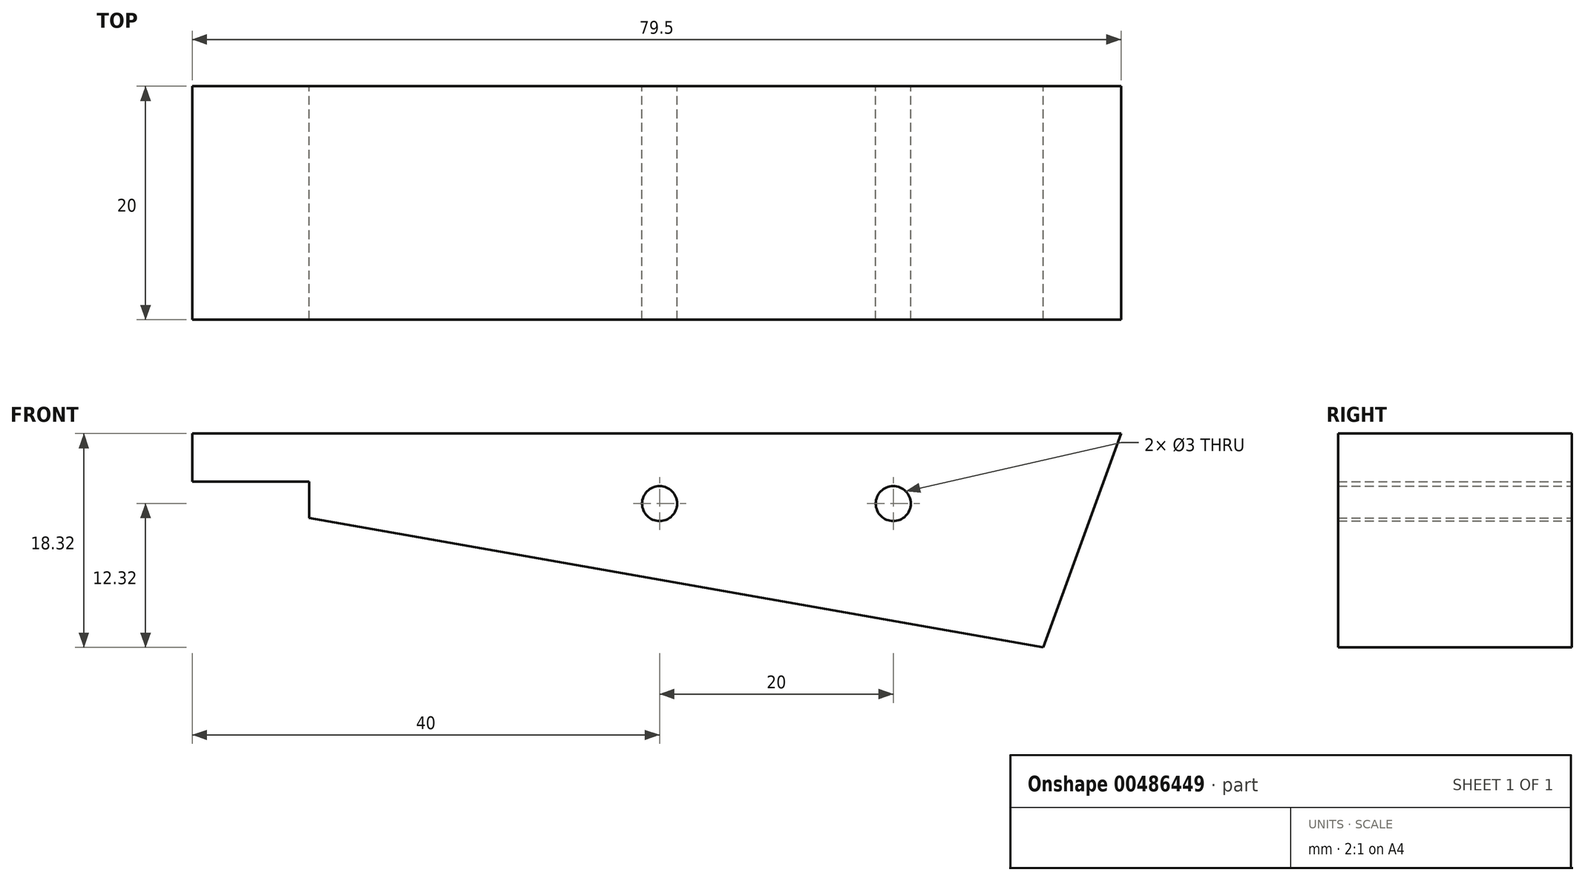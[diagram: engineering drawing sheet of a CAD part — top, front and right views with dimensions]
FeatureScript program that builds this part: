
annotation { "Feature Type Name" : "Feature", "Feature Type Description" : "" }
export const myFeature = defineFeature(function(context is Context, id is Id, definition is map)
    precondition{}
    {
        {
            var Q0;
            Q0=qCreatedBy(makeId("Front.planeOp"),FACE);
            var sketch = newSketch(context, id + "F0", { "sketchPlane" : qUnion([Q0])});
            skLineSegment(sketch, "E0", {"start": v(0, 0) * mm, "end": v(79.5, 0) * mm});
            skLineSegment(sketch, "E1", {"start": v(79.5, 0) * mm, "end": v(72.83, -18.32) * mm});
            skLineSegment(sketch, "E2", {"start": v(72.83, -18.32) * mm, "end": v(10, -7.25) * mm});
            skLineSegment(sketch, "E3", {"start": v(10, -7.25) * mm, "end": v(10, -4.12) * mm});
            skLineSegment(sketch, "E4", {"start": v(10, -4.12) * mm, "end": v(0, -4.12) * mm});
            skLineSegment(sketch, "E5", {"start": v(0, -4.12) * mm, "end": v(0, 0) * mm});
            skCircle(sketch, "E6", {"center": v(40, -6) * mm, "radius": 1.5 * mm});
            skCircle(sketch, "E7", {"center": v(60, -6) * mm, "radius": 1.5 * mm});
            skSolve(sketch);
        }
        {
            var Q0;
            Q0=makeQuery(id+"F0.imprint","IMPRINT",FACE,{"disambiguationData":[TD([[makeQuery(id+"F0.imprint","IMPRINT",EDGE,{"derivedFrom":sQuery(id+"F0.wireOp",EDGE,"E0")}),-1.0]])]});
            extrude(context, id + "F1", {"entities" : qUnion([Q0]), "endBound" : BoundingType.SYMMETRIC, "depth" : 20 * mm, "offsetDistance" : 25 * mm});
        }
    });
